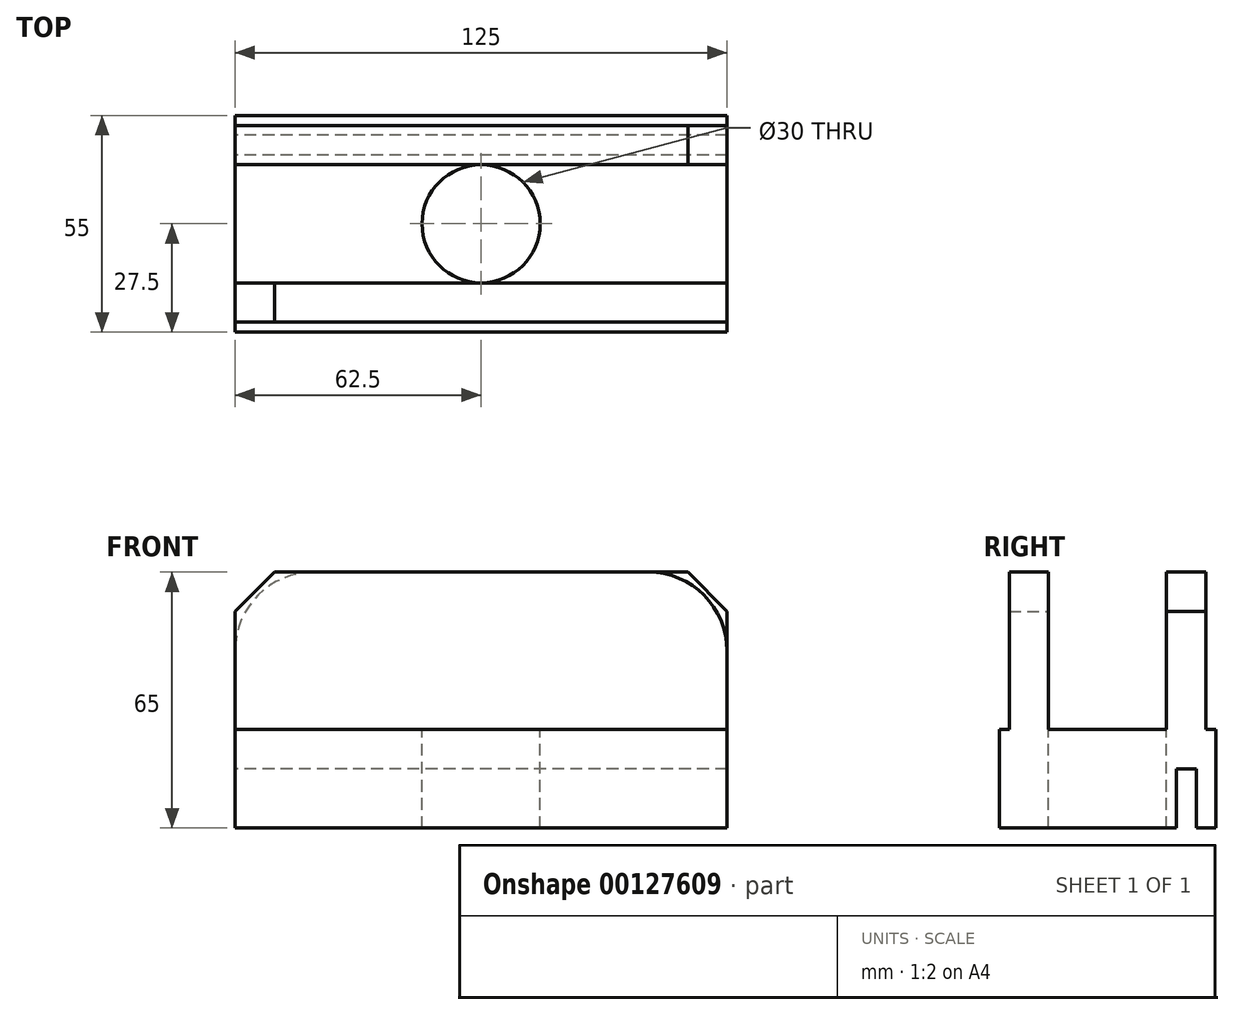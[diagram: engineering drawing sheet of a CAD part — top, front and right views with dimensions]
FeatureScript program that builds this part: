
annotation { "Feature Type Name" : "Feature", "Feature Type Description" : "" }
export const myFeature = defineFeature(function(context is Context, id is Id, definition is map)
    precondition{}
    {
        {
            var Q0;
            Q0=qCreatedBy(makeId("Front.planeOp"),FACE);
            var sketch = newSketch(context, id + "F0", { "sketchPlane" : qUnion([Q0])});
            skLineSegment(sketch, "E0.bottom", {"start": v(62.5, -12.5) * mm, "end": v(-62.5, -12.5) * mm});
            skLineSegment(sketch, "E0.top", {"start": v(62.5, 12.5) * mm, "end": v(-62.5, 12.5) * mm});
            skLineSegment(sketch, "E0.left", {"start": v(62.5, -12.5) * mm, "end": v(62.5, 12.5) * mm});
            skLineSegment(sketch, "E0.right", {"start": v(-62.5, -12.5) * mm, "end": v(-62.5, 12.5) * mm});
            skPoint(sketch, "E0.middle", {"position": v(0, 0) * mm});
            skSolve(sketch);
        }
        {
            var Q0;
            Q0 = qSketchRegion(id + "F0", true);
            extrude(context, id + "F1", {"entities" : qUnion([Q0]), "depth" : 55 * mm});
        }
        {
            var Q0;
            Q0=makeQuery(id+"F1.opExtrude","CAP_FACE",FACE,{"disambiguationData":[OSD([sQuery(id+"F0.wireOp",EDGE,"E0.bottom"),sQuery(id+"F0.wireOp",EDGE,"E0.top"),sQuery(id+"F0.wireOp",EDGE,"E0.left"),sQuery(id+"F0.wireOp",EDGE,"E0.right")])],"isStart":false});
            var sketch = newSketch(context, id + "F2", { "sketchPlane" : qUnion([Q0])});
            skLineSegment(sketch, "E1.bottom", {"start": v(62.5, 52.5) * mm, "end": v(-62.5, 52.5) * mm});
            skLineSegment(sketch, "E1.top", {"start": v(62.5, 12.5) * mm, "end": v(-62.5, 12.5) * mm});
            skLineSegment(sketch, "E1.left", {"start": v(62.5, 52.5) * mm, "end": v(62.5, 12.5) * mm});
            skLineSegment(sketch, "E1.right", {"start": v(-62.5, 52.5) * mm, "end": v(-62.5, 12.5) * mm});
            skSolve(sketch);
        }
        {
            var Q0;
            Q0 = qSketchRegion(id + "F2", true);
            extrude(context, id + "F3", {"entities" : qUnion([Q0]), "operationType" : NewBodyOperationType.ADD, "oppositeDirection" : true, "depth" : 52.5 * mm});
        }
        {
            var Q0;
            Q0=makeQuery(id+"F3.boolean.opBoolean","MERGE",FACE,{"derivedFrom":[makeQuery(id+"F1.opExtrude","CAP_FACE",FACE,{"disambiguationData":[OSD([sQuery(id+"F0.wireOp",EDGE,"E0.bottom"),sQuery(id+"F0.wireOp",EDGE,"E0.top"),sQuery(id+"F0.wireOp",EDGE,"E0.left"),sQuery(id+"F0.wireOp",EDGE,"E0.right")])],"isStart":false}),makeQuery(id+"F3.opExtrude","CAP_FACE",FACE,{"disambiguationData":[OSD([sQuery(id+"F2.wireOp",EDGE,"E1.bottom"),sQuery(id+"F2.wireOp",EDGE,"E1.top"),sQuery(id+"F2.wireOp",EDGE,"E1.left"),sQuery(id+"F2.wireOp",EDGE,"E1.right")])],"isStart":true})]});
            var sketch = newSketch(context, id + "F4", { "sketchPlane" : qUnion([Q0])});
            skLineSegment(sketch, "E2.bottom", {"start": v(62.5, 12.5) * mm, "end": v(-62.5, 12.5) * mm});
            skLineSegment(sketch, "E2.top", {"start": v(62.5, 52.5) * mm, "end": v(-62.5, 52.5) * mm});
            skLineSegment(sketch, "E2.left", {"start": v(62.5, 12.5) * mm, "end": v(62.5, 52.5) * mm});
            skLineSegment(sketch, "E2.right", {"start": v(-62.5, 12.5) * mm, "end": v(-62.5, 52.5) * mm});
            skSolve(sketch);
        }
        {
            var Q0;
            Q0 = qSketchRegion(id + "F4", true);
            extrude(context, id + "F5", {"entities" : qUnion([Q0]), "operationType" : NewBodyOperationType.REMOVE, "oppositeDirection" : true, "depth" : 2.5 * mm});
        }
        {
            var Q0;
            Q0=makeQuery(id+"F3.boolean.opBoolean","MERGE",FACE,{"derivedFrom":[makeQuery(id+"F1.opExtrude","SWEPT_FACE",FACE,{"disambiguationData":[OSD([sQuery(id+"F0.wireOp",EDGE,"E0.right")])]}),makeQuery(id+"F3.opExtrude","SWEPT_FACE",FACE,{"disambiguationData":[OSD([sQuery(id+"F2.wireOp",EDGE,"E1.right")])]})]});
            var sketch = newSketch(context, id + "F6", { "sketchPlane" : qUnion([Q0])});
            skLineSegment(sketch, "E3", {"start": v(12.5, 52.5) * mm, "end": v(12.5, 12.5) * mm});
            skLineSegment(sketch, "E4", {"start": v(12.5, 12.5) * mm, "end": v(42.5, 12.5) * mm});
            skLineSegment(sketch, "E5", {"start": v(42.5, 12.5) * mm, "end": v(42.5, 52.5) * mm});
            skLineSegment(sketch, "E6", {"start": v(12.5, 52.5) * mm, "end": v(42.5, 52.5) * mm});
            skSolve(sketch);
        }
        {
            var Q0;
            Q0 = qSketchRegion(id + "F6", true);
            extrude(context, id + "F7", {"entities" : qUnion([Q0]), "operationType" : NewBodyOperationType.REMOVE, "endBound" : BoundingType.THROUGH_ALL, "oppositeDirection" : true, "depth" : 25 * mm});
        }
        {
            var Q0;
            {var subQ0=sQuery(id+"F2.wireOp",EDGE,"E1.bottom");var subQ1=sQuery(id+"F2.wireOp",EDGE,"E1.right");Q0=makeQuery(id+"F7.boolean.opBoolean","SPLIT",EDGE,{"disambiguationData":[TD([makeQuery(id+"F7.opExtrude","SWEPT_FACE",FACE,{"disambiguationData":[OSD([sQuery(id+"F6.wireOp",EDGE,"E5")])]})])],"derivedFrom":makeQuery(id+"F3.opExtrude","SWEPT_EDGE",EDGE,{"disambiguationData":[OSD([subQ0,subQ1])]})});}
            chamfer(context, id + "F8", {"entities" : qUnion([Q0]), "width" : 10 * mm, "tangentPropagation" : true});
        }
        {
            var Q0;
            {var subQ0=sQuery(id+"F2.wireOp",EDGE,"E1.right");var subQ1=sQuery(id+"F2.wireOp",EDGE,"E1.bottom");Q0=makeQuery(id+"F7.boolean.opBoolean","SPLIT",EDGE,{"disambiguationData":[TD([makeQuery(id+"F7.opExtrude","SWEPT_FACE",FACE,{"disambiguationData":[OSD([sQuery(id+"F6.wireOp",EDGE,"E3")])]})])],"derivedFrom":makeQuery(id+"F3.opExtrude","SWEPT_EDGE",EDGE,{"disambiguationData":[OSD([subQ1,subQ0])]})});}
            fillet(context, id + "F9", {"entities" : qUnion([Q0]), "radius" : 20 * mm, "tangentPropagation" : true, "allowEdgeOverflow" : false});
        }
        {
            var Q0;
            {var subQ0=sQuery(id+"F2.wireOp",EDGE,"E1.left");var subQ1=sQuery(id+"F2.wireOp",EDGE,"E1.bottom");Q0=makeQuery(id+"F7.boolean.opBoolean","SPLIT",EDGE,{"disambiguationData":[TD([makeQuery(id+"F7.opExtrude","SWEPT_FACE",FACE,{"disambiguationData":[OSD([sQuery(id+"F6.wireOp",EDGE,"E3")])]})])],"derivedFrom":makeQuery(id+"F3.opExtrude","SWEPT_EDGE",EDGE,{"disambiguationData":[OSD([subQ1,subQ0])]})});}
            chamfer(context, id + "F10", {"entities" : qUnion([Q0]), "width" : 10 * mm, "tangentPropagation" : true});
        }
        {
            var Q0;
            {var subQ0=sQuery(id+"F2.wireOp",EDGE,"E1.bottom");var subQ1=sQuery(id+"F2.wireOp",EDGE,"E1.left");Q0=makeQuery(id+"F7.boolean.opBoolean","SPLIT",EDGE,{"disambiguationData":[TD([makeQuery(id+"F7.opExtrude","SWEPT_FACE",FACE,{"disambiguationData":[OSD([sQuery(id+"F6.wireOp",EDGE,"E5")])]})])],"derivedFrom":makeQuery(id+"F3.opExtrude","SWEPT_EDGE",EDGE,{"disambiguationData":[OSD([subQ0,subQ1])]})});}
            fillet(context, id + "F11", {"entities" : qUnion([Q0]), "radius" : 20 * mm, "tangentPropagation" : true, "allowEdgeOverflow" : false});
        }
        {
            var Q0;
            Q0=makeQuery(id+"F3.boolean.opBoolean","MERGE",FACE,{"derivedFrom":[makeQuery(id+"F1.opExtrude","SWEPT_FACE",FACE,{"disambiguationData":[OSD([sQuery(id+"F0.wireOp",EDGE,"E0.right")])]}),makeQuery(id+"F3.opExtrude","SWEPT_FACE",FACE,{"disambiguationData":[OSD([sQuery(id+"F2.wireOp",EDGE,"E1.right")])]})]});
            var sketch = newSketch(context, id + "F12", { "sketchPlane" : qUnion([Q0])});
            skLineSegment(sketch, "E7", {"start": v(5, 2.5) * mm, "end": v(5, -12.5) * mm});
            skLineSegment(sketch, "E8", {"start": v(5, -12.5) * mm, "end": v(10, -12.5) * mm});
            skLineSegment(sketch, "E9", {"start": v(10, -12.5) * mm, "end": v(10, 2.5) * mm});
            skLineSegment(sketch, "E10", {"start": v(10, 2.5) * mm, "end": v(5, 2.5) * mm});
            skSolve(sketch);
        }
        {
            var Q0;
            Q0=makeQuery(id+"F12.imprint","IMPRINT",FACE,{"disambiguationData":[TD([[makeQuery(id+"F12.imprint","IMPRINT",EDGE,{"derivedFrom":sQuery(id+"F12.wireOp",EDGE,"E7")}),1.0]])]});
            extrude(context, id + "F13", {"entities" : qUnion([Q0]), "operationType" : NewBodyOperationType.REMOVE, "endBound" : BoundingType.THROUGH_ALL, "oppositeDirection" : true, "depth" : 25 * mm});
        }
        {
            var Q0;
            Q0=makeQuery(id+"F7.boolean.opBoolean","COPY",FACE,{"derivedFrom":makeQuery(id+"F7.opExtrude","SWEPT_FACE",FACE,{"disambiguationData":[OSD([sQuery(id+"F6.wireOp",EDGE,"E4")])]})});
            var sketch = newSketch(context, id + "F14", { "sketchPlane" : qUnion([Q0])});
            skCircle(sketch, "E11", {"center": v(0, -27.5) * mm, "radius": 15 * mm});
            skSolve(sketch);
        }
        {
            var Q0;
            {var subQ0=sQuery(id+"F14.wireOp",EDGE,"E11");var subQ1=sQuery(id+"F6.wireOp",EDGE,"E4");var subQ2=makeQuery(id+"F14.imprint","INTERSECT",VERTEX,{"derivedFrom":[makeQuery(id+"F7.boolean.opBoolean","COPY",EDGE,{"derivedFrom":makeQuery(id+"F7.opExtrude","SWEPT_EDGE",EDGE,{"disambiguationData":[OSD([sQuery(id+"F6.wireOp",EDGE,"E3"),subQ1])]})}),subQ0]});Q0=makeQuery(id+"F14.imprint","IMPRINT",FACE,{"disambiguationData":[TD([[makeQuery(id+"F14.imprint","IMPRINT",EDGE,{"disambiguationData":[TD([[subQ2,-1.0]])],"derivedFrom":subQ0}),1.0]])]});}
            extrude(context, id + "F15", {"entities" : qUnion([Q0]), "operationType" : NewBodyOperationType.REMOVE, "endBound" : BoundingType.THROUGH_ALL, "oppositeDirection" : true, "depth" : 25 * mm});
        }
    });
